# Revit family: spectral_stora_stora-ra-led_4300_840_os_5369
name_source: partatom
category: Lighting Fixtures
revit_build: Autodesk Revit 2016 (Build: 20150220_1215(x64)
units: mm (PartAtom-declared; Revit-internal decimal feet)

## family parameters
Cut with Voids When Loaded = No
Host = Face
Light Source = No
Part Type = Normal
Room Calculation Point = No
Round Connector Dimension = Use Diameter
Shared = No

## types (1)
- SPECTRAL STORA (1 x )
    Apparent Load = 0 VA
    CIE Flux Codes = 48 78 95 100 100
    Control Gear = Electronic transformer
    Default Elevation = 1800 mm
    Description = SPC0620006
STORA surface mounted LED luminaire

Design:
Round luminaire element with an opal acrylic panel mounted in a profile 
frame made of power-coated aluminium. The frame is fastened on the powdercoated steel body using a bayonet catch with spring clip. The steel body houses the electrical components and electronic ballast. The LED module is formed as a round LED flat board and can be removed for mounting or exchange using a keyhole screw connection. Plug-in electrical connection of the LED flat board. The luminaire is configured with heat-resistant wiring. Homogeneous illumination of the light surface. Suitable for ceiling or wall mounting. Light colour 4000 K. Also in a dimmable version. Protection rating IP20, safety class I.

Colour:
Frame – similar to RAL 9016 white silk matt
    Height = 60 mm
    Lamp = 1 x
    Lamp count = 1
    Length = 422 mm
    Luminous efficacy = 0 lm/W
    Manufacturer = Ridi
    ModVariant = No
    Model = STORA-RA-LED 4300/840 OS
    Number of Poles = 1
    OnlyDefault = Yes
    Power Factor = 1
    Product Name = SPECTRAL STORA
    Product group = Ceiling / wall-mounted luminaires
    ProductGroupID = 30
    Protection Class = Protection class
    Protection Degree = Degree of protection
    RlxData = <blob elided: 12289 chars, md5=8ef36354>
    Socket = socket
    Standby Power = 0 W
    System Light Flux = 0 lm
    System Power = 0 W
    Type Image = stora-ra.jpg
    URL = http://reluxnet.relux.com
    VarID = 1
    Voltage = 0 V
    Weight = 0.00 kg
    Width = 0 mm  [stored 0 ft]

note: [stored X ft] marks values corroborated as IEEE doubles in the binary element streams (Revit-internal decimal feet)

## geometry (parser evidence)
native form markers: Sweep x8
no freeform markers — native parametric forms only
